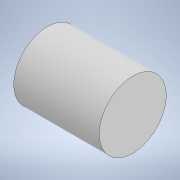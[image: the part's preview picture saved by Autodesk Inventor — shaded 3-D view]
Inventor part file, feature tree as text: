
AUTODESK INVENTOR PART (.ipt)
format: ipt  version: 2020.2 (Build 242310000, 310)  size: 90,624 bytes
history: native  units: mm
features: extrude x1, sketch x1
ambient origin geometry x8: Origin, YZ Plane, XZ Plane, XY Plane, X Axis, Y Axis, Z Axis, Center Point
bodies: Solid1 (feature_tree)
feature tree (2):
  extrude  "Extrusion1"  Depth=11.5mm TaperAngle=0.0deg
  sketch  "Sketch1"  dims[d0=9.0mm d1=11.5mm d2=0.0mm]
